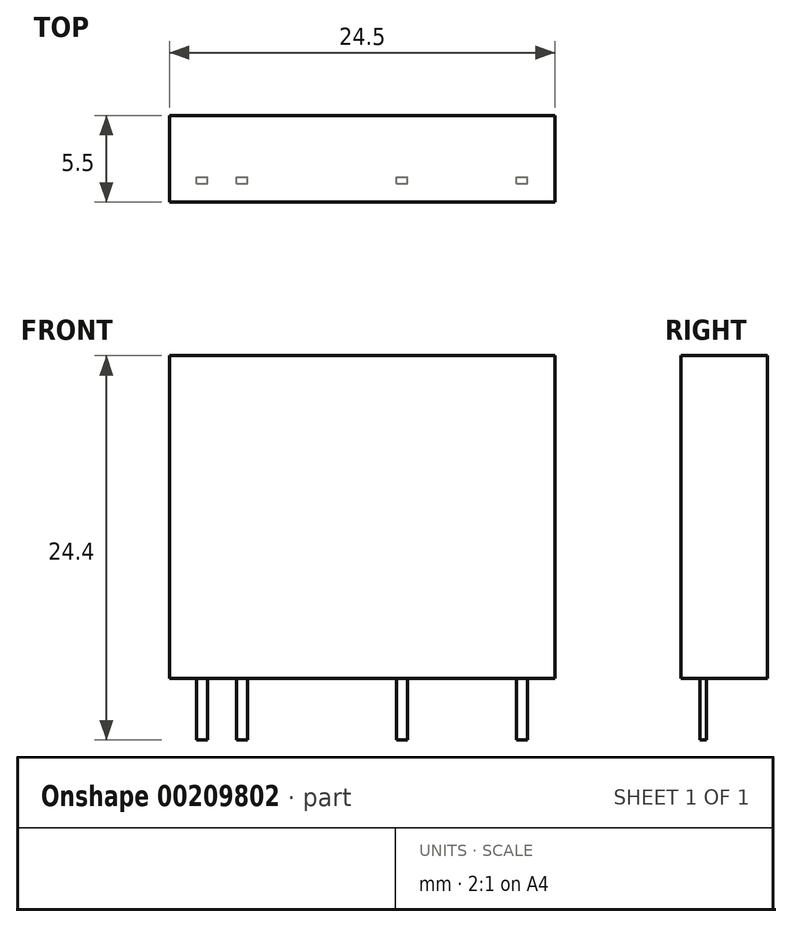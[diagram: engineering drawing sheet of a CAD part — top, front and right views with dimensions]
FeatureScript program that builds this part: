
annotation { "Feature Type Name" : "Feature", "Feature Type Description" : "" }
export const myFeature = defineFeature(function(context is Context, id is Id, definition is map)
    precondition{}
    {
        {
            var Q0;
            Q0=qCreatedBy(makeId("Top.planeOp"),FACE);
            var sketch = newSketch(context, id + "F0", { "sketchPlane" : qUnion([Q0]) });
            skLineSegment(sketch, "E0.bottom", {"start": v(-12.25, 4.1) * mm, "end": v(12.25, 4.1) * mm});
            skLineSegment(sketch, "E0.top", {"start": v(-12.25, -1.4) * mm, "end": v(12.25, -1.4) * mm});
            skLineSegment(sketch, "E0.left", {"start": v(-12.25, 4.1) * mm, "end": v(-12.25, -1.4) * mm});
            skLineSegment(sketch, "E0.right", {"start": v(12.25, 4.1) * mm, "end": v(12.25, -1.4) * mm});
            skLineSegment(sketch, "E1.bottom", {"start": v(-10.5, -0.2) * mm, "end": v(-9.8, -0.2) * mm});
            skLineSegment(sketch, "E1.top", {"start": v(-10.5, 0.2) * mm, "end": v(-9.8, 0.2) * mm});
            skLineSegment(sketch, "E1.left", {"start": v(-10.5, -0.2) * mm, "end": v(-10.5, 0.2) * mm});
            skLineSegment(sketch, "E1.right", {"start": v(-9.8, -0.2) * mm, "end": v(-9.8, 0.2) * mm});
            skPoint(sketch, "E2", {"position": v(-10.16, 0) * mm});
            skLineSegment(sketch, "E3", {"start": v(-12.25, 0) * mm, "end": v(12.25, 0) * mm, "construction": true});
            skPoint(sketch, "E4", {"position": v(-7.62, 0) * mm});
            skPoint(sketch, "E5", {"position": v(2.54, 0) * mm});
            skPoint(sketch, "E6", {"position": v(10.16, 0) * mm});
            skLineSegment(sketch, "E7", {"start": v(-10.16, -0.2) * mm, "end": v(-10.16, 0.2) * mm, "construction": true});
            skLineSegment(sketch, "E8.bottom", {"start": v(-7.97, -0.2) * mm, "end": v(-7.27, -0.2) * mm});
            skLineSegment(sketch, "E8.top", {"start": v(-7.97, 0.2) * mm, "end": v(-7.27, 0.2) * mm});
            skLineSegment(sketch, "E8.left", {"start": v(-7.97, -0.2) * mm, "end": v(-7.97, 0.2) * mm});
            skLineSegment(sketch, "E8.right", {"start": v(-7.27, -0.2) * mm, "end": v(-7.27, 0.2) * mm});
            skLineSegment(sketch, "E9.bottom", {"start": v(2.19, -0.2) * mm, "end": v(2.9, -0.2) * mm});
            skLineSegment(sketch, "E9.top", {"start": v(2.19, 0.2) * mm, "end": v(2.9, 0.2) * mm});
            skLineSegment(sketch, "E9.left", {"start": v(2.19, -0.2) * mm, "end": v(2.19, 0.2) * mm});
            skLineSegment(sketch, "E9.right", {"start": v(2.9, -0.2) * mm, "end": v(2.9, 0.2) * mm});
            skLineSegment(sketch, "E10.bottom", {"start": v(9.8, -0.2) * mm, "end": v(10.5, -0.2) * mm});
            skLineSegment(sketch, "E10.top", {"start": v(9.8, 0.2) * mm, "end": v(10.5, 0.2) * mm});
            skLineSegment(sketch, "E10.left", {"start": v(9.8, -0.2) * mm, "end": v(9.8, 0.2) * mm});
            skLineSegment(sketch, "E10.right", {"start": v(10.5, -0.2) * mm, "end": v(10.5, 0.2) * mm});
            skLineSegment(sketch, "E11", {"start": v(-7.62, -0.2) * mm, "end": v(-7.62, 0.2) * mm, "construction": true});
            skLineSegment(sketch, "E12", {"start": v(2.54, -0.2) * mm, "end": v(2.54, 0.2) * mm, "construction": true});
            skLineSegment(sketch, "E13", {"start": v(10.16, -0.2) * mm, "end": v(10.16, 0.2) * mm, "construction": true});
            skSolve(sketch);
        }
        {
            var Q0;
            Q0=makeQuery(id+"F0.imprint","IMPRINT",FACE,{"disambiguationData":[TD([[makeQuery(id+"F0.imprint","IMPRINT",EDGE,{"derivedFrom":sQuery(id+"F0.wireOp",EDGE,"E1.bottom")}),1.0]])]});
            var Q1;
            Q1=makeQuery(id+"F0.imprint","IMPRINT",FACE,{"disambiguationData":[TD([[makeQuery(id+"F0.imprint","IMPRINT",EDGE,{"derivedFrom":sQuery(id+"F0.wireOp",EDGE,"E0.bottom")}),-1.0]])]});
            var Q2;
            Q2=makeQuery(id+"F0.imprint","IMPRINT",FACE,{"disambiguationData":[TD([[makeQuery(id+"F0.imprint","IMPRINT",EDGE,{"derivedFrom":sQuery(id+"F0.wireOp",EDGE,"E9.bottom")}),1.0]])]});
            var Q3;
            Q3=makeQuery(id+"F0.imprint","IMPRINT",FACE,{"disambiguationData":[TD([[makeQuery(id+"F0.imprint","IMPRINT",EDGE,{"derivedFrom":sQuery(id+"F0.wireOp",EDGE,"E10.bottom")}),1.0]])]});
            var Q4;
            Q4=makeQuery(id+"F0.imprint","IMPRINT",FACE,{"disambiguationData":[TD([[makeQuery(id+"F0.imprint","IMPRINT",EDGE,{"derivedFrom":sQuery(id+"F0.wireOp",EDGE,"E8.bottom")}),1.0]])]});
            extrude(context, id + "F1", {"entities" : qUnion([Q0, Q1, Q2, Q3, Q4]), "depth" : 20.5 * mm});
        }
        {
            var Q0;
            Q0=makeQuery(id+"F0.imprint","IMPRINT",FACE,{"disambiguationData":[TD([[makeQuery(id+"F0.imprint","IMPRINT",EDGE,{"derivedFrom":sQuery(id+"F0.wireOp",EDGE,"E1.bottom")}),1.0]])]});
            var Q1;
            Q1=makeQuery(id+"F0.imprint","IMPRINT",FACE,{"disambiguationData":[TD([[makeQuery(id+"F0.imprint","IMPRINT",EDGE,{"derivedFrom":sQuery(id+"F0.wireOp",EDGE,"E8.bottom")}),1.0]])]});
            var Q2;
            Q2=makeQuery(id+"F0.imprint","IMPRINT",FACE,{"disambiguationData":[TD([[makeQuery(id+"F0.imprint","IMPRINT",EDGE,{"derivedFrom":sQuery(id+"F0.wireOp",EDGE,"E9.bottom")}),1.0]])]});
            var Q3;
            Q3=makeQuery(id+"F0.imprint","IMPRINT",FACE,{"disambiguationData":[TD([[makeQuery(id+"F0.imprint","IMPRINT",EDGE,{"derivedFrom":sQuery(id+"F0.wireOp",EDGE,"E10.bottom")}),1.0]])]});
            extrude(context, id + "F2", {"entities" : qUnion([Q0, Q1, Q2, Q3]), "oppositeDirection" : true, "depth" : 3.9 * mm});
        }
    });
